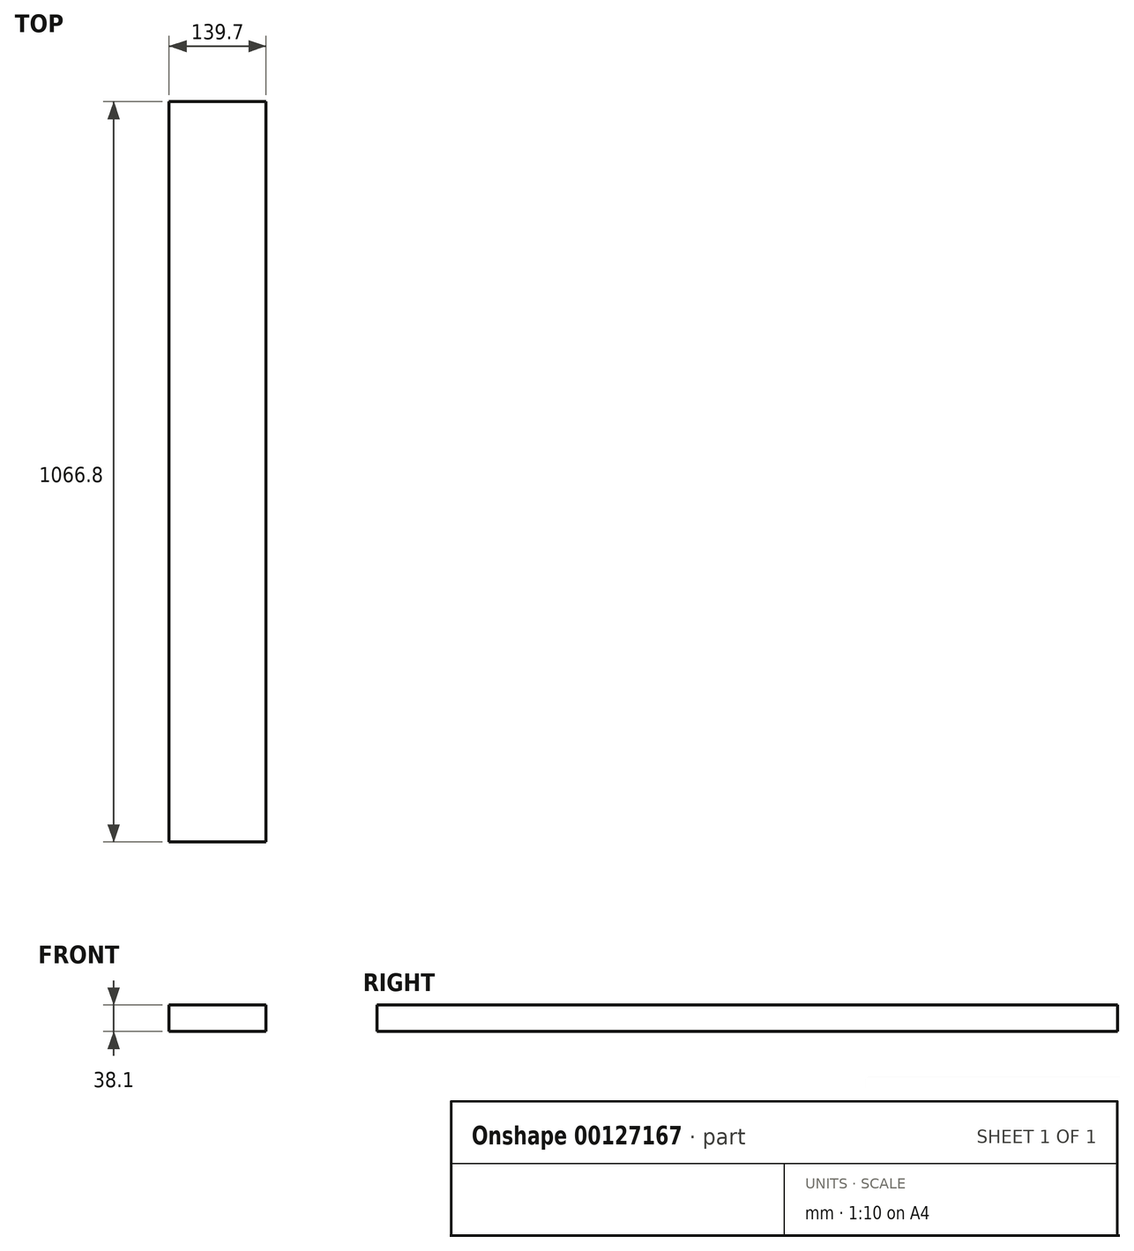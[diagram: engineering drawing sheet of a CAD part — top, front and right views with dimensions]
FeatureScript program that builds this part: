
annotation { "Feature Type Name" : "Feature", "Feature Type Description" : "" }
export const myFeature = defineFeature(function(context is Context, id is Id, definition is map)
    precondition{}
    {
        {
            var Q0;
            Q0=qCreatedBy(makeId("Front.planeOp"),FACE);
            var sketch = newSketch(context, id + "F0", { "sketchPlane" : qUnion([Q0])});
            skLineSegment(sketch, "E0.bottom", {"start": v(69.85, -19.05) * mm, "end": v(-69.85, -19.05) * mm});
            skLineSegment(sketch, "E0.top", {"start": v(69.85, 19.05) * mm, "end": v(-69.85, 19.05) * mm});
            skLineSegment(sketch, "E0.left", {"start": v(69.85, -19.05) * mm, "end": v(69.85, 19.05) * mm});
            skLineSegment(sketch, "E0.right", {"start": v(-69.85, -19.05) * mm, "end": v(-69.85, 19.05) * mm});
            skPoint(sketch, "E0.middle", {"position": v(0, 0) * mm});
            skSolve(sketch);
        }
        {
            var Q0;
            Q0=qSketchRegion(id+"F0",true);
            extrude(context, id + "F1", {"entities" : qUnion([Q0]), "depth" : 1066.8 * mm});
        }
    });
